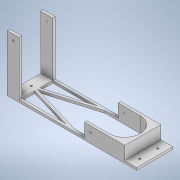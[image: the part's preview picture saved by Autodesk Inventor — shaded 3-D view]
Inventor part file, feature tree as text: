
AUTODESK INVENTOR PART (.ipt)
format: ipt  version: 2020 (Build 240168000, 168)  size: 248,320 bytes
history: native  units: mm
features: sketch x5, extrude x3, other x2, hole x2, mirror x1
ambient origin geometry x8: Origin, YZ Plane, XZ Plane, XY Plane, X Axis, Y Axis, Z Axis, Center Point
bodies: Body1 (feature_tree)
feature tree (13):
  other  "Твердое тело1"
  extrude  "Выдавливание1"  Depth=108.0mm
  extrude  "Выдавливание2"  Depth=10.0mm
  extrude  "Выдавливание4"  Depth=5.0mm
  hole  "Отверстие1"  [1 undecoded]
  mirror  "Зеркальное отражение1"
  hole  "Отверстие2"  [1 undecoded]
  sketch  "Эскиз1"
  sketch  "Эскиз2"
  sketch  "Эскиз3"
  sketch  "Эскиз4"
  sketch  "Эскиз5"
  other  "Проецирование ребер1"
note: 2 required parameter values undecoded (feature->parameter linkage not recoverable at this tier; creation-order binding heuristic only, values carry confidence <= 0.55)
